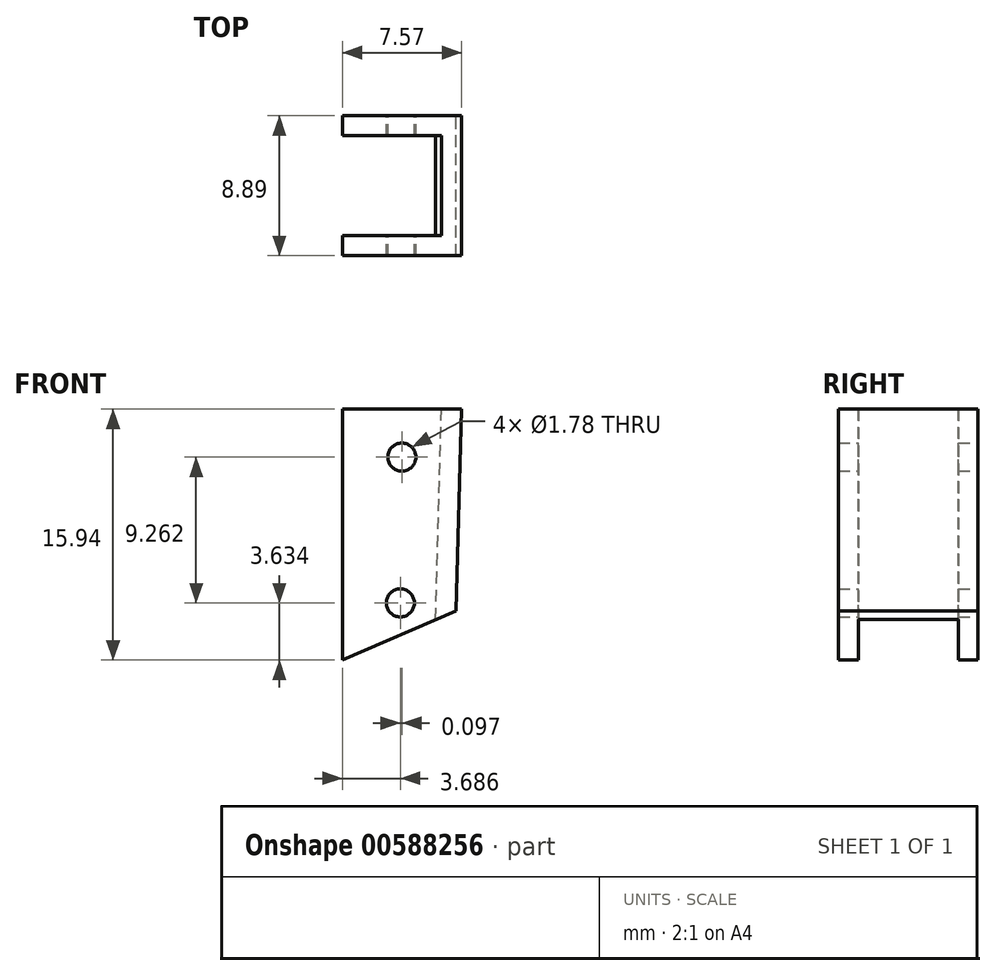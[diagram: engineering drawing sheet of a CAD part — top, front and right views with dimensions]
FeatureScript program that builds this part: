
annotation { "Feature Type Name" : "Feature", "Feature Type Description" : "" }
export const myFeature = defineFeature(function(context is Context, id is Id, definition is map)
    precondition{}
    {
        {
            var Q0;
            Q0=qCreatedBy(makeId("Front.planeOp"),FACE);
            var sketch = newSketch(context, id + "F0", { "sketchPlane" : qUnion([Q0])});
            skLineSegment(sketch, "E0", {"start": v(-45.51, 46.38) * mm, "end": v(-53.08, 46.38) * mm});
            skLineSegment(sketch, "E1", {"start": v(-53.08, 46.38) * mm, "end": v(-53.08, 30.44) * mm});
            skPoint(sketch, "E2", {"position": v(-49.3, 43.34) * mm});
            skPoint(sketch, "E3", {"position": v(-49.4, 34.07) * mm});
            skPoint(sketch, "E4", {"position": v(-49.3, 46.38) * mm});
            skPoint(sketch, "E5", {"position": v(-49.4, 30.44) * mm});
            skLineSegment(sketch, "E6", {"start": v(-53.08, 30.44) * mm, "end": v(-45.87, 33.57) * mm});
            skLineSegment(sketch, "E7", {"start": v(-45.87, 33.57) * mm, "end": v(-45.51, 46.38) * mm});
            skSolve(sketch);
        }
        {
            var Q0;
            Q0=makeQuery(id+"F0.imprint","IMPRINT",FACE,{"disambiguationData":[TD([[makeQuery(id+"F0.imprint","IMPRINT",EDGE,{"derivedFrom":sQuery(id+"F0.wireOp",EDGE,"4fXO96kz-Lxmm-tUBH-iLiP-RmEOZpFtSm0h")}),1.0]])]});
            var Q1;
            Q1=makeQuery(id+"F0.imprint","IMPRINT",FACE,{"disambiguationData":[TD([[makeQuery(id+"F0.imprint","IMPRINT",EDGE,{"derivedFrom":sQuery(id+"F0.wireOp",EDGE,"E0")}),1.0]])]});
            extrude(context, id + "F1", {"entities" : qUnion([Q0, Q1]), "depth" : 8.9 * mm, "offsetDistance" : 25.4 * mm});
        }
        {
            var Q0;
            Q0=makeQuery(id+"F1.opExtrude","SWEPT_FACE",FACE,{"disambiguationData":[OSD([sQuery(id+"F0.wireOp",EDGE,"E0")])]});
            var Q1;
            Q1=makeQuery(id+"F1.opExtrude","SWEPT_FACE",FACE,{"disambiguationData":[OSD([sQuery(id+"F0.wireOp",EDGE,"E1")])]});
            var Q2;
            Q2=makeQuery(id+"F1.opExtrude","SWEPT_FACE",FACE,{"disambiguationData":[OSD([sQuery(id+"F0.wireOp",EDGE,"4fXO96kz-Lxmm-tUBH-iLiP-RmEOZpFtSm0h")])]});
            var Q3;
            Q3=makeQuery(id+"F1.opExtrude","SWEPT_FACE",FACE,{"disambiguationData":[OSD([sQuery(id+"F0.wireOp",EDGE,"E6")])]});
            shell(context, id + "F2", {"entities" : qUnion([Q0, Q1, Q2, Q3]), "thickness" : 1.27 * mm});
        }
        {
            var Q0;
            Q0=sQuery(id+"F0.wireOp",VERTEX,"E2");
            var Q1;
            Q1=sQuery(id+"F0.wireOp",VERTEX,"E3");
            var Q2;
            Q2=makeQuery(id+"F1.opExtrude","SWEPT_BODY",BODY,{"disambiguationData":[OSD([sQuery(id+"F0.wireOp",EDGE,"E0"),sQuery(id+"F0.wireOp",EDGE,"E1"),sQuery(id+"F0.wireOp",EDGE,"E6"),sQuery(id+"F0.wireOp",EDGE,"E7")])]});
            hole(context, id + "F3", {"style" : HoleStyle.SIMPLE, "endStyle" : HoleEndStyle.THROUGH, "oppositeDirection" : true, "holeDiameter" : 1.78 * mm, "majorDiameter" : 6.35 * mm, "isTappedThrough" : true, "tappedDepth" : 12.7 * mm, "tapClearance" : 3, "locations" : qUnion([Q0, Q1]), "scope" : qUnion([Q2])});
        }
    });
